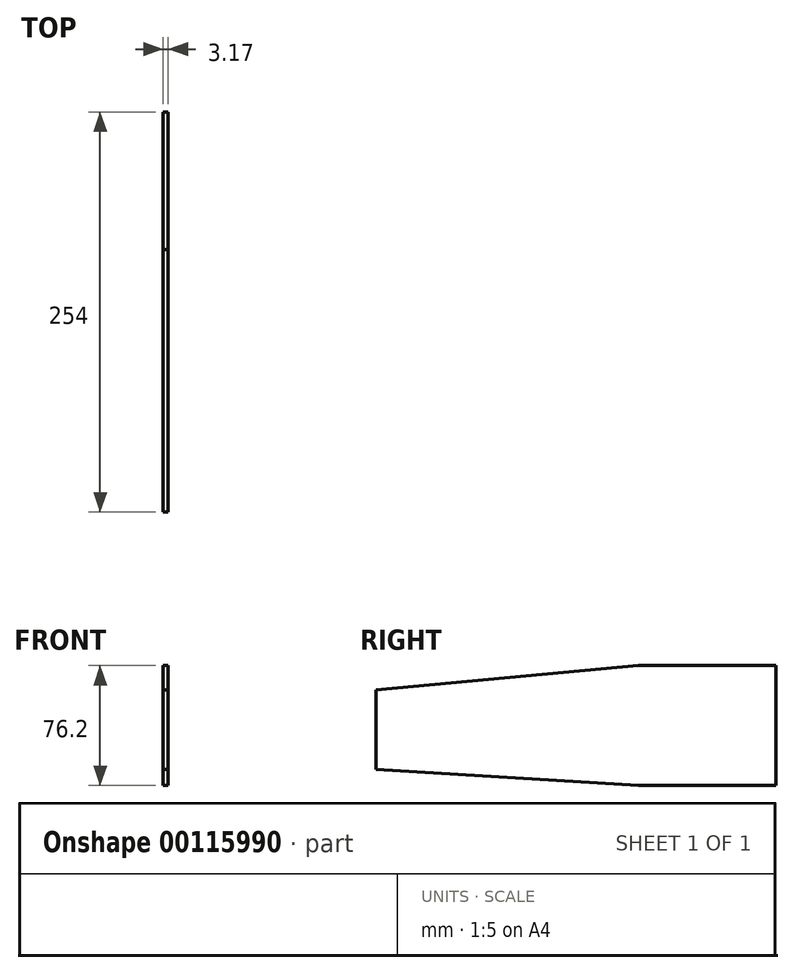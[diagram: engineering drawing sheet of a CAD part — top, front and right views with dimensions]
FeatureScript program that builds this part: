
annotation { "Feature Type Name" : "Feature", "Feature Type Description" : "" }
export const myFeature = defineFeature(function(context is Context, id is Id, definition is map)
    precondition{}
    {
        {
            var Q0;
            Q0=qCreatedBy(makeId("Right.planeOp"),FACE);
            var sketch = newSketch(context, id + "F0", { "sketchPlane" : qUnion([Q0])});
            skLineSegment(sketch, "E0", {"start": v(-5.73, 56) * mm, "end": v(-172.52, 40.6) * mm});
            skLineSegment(sketch, "E1.MirrorCS", {"start": v(-5.73, -20.2) * mm, "end": v(-172.52, -10) * mm});
            skLineSegment(sketch, "E2.bottom", {"start": v(-5.73, 56) * mm, "end": v(81.48, 56) * mm});
            skLineSegment(sketch, "E2.top", {"start": v(-5.73, -20.2) * mm, "end": v(81.48, -20.2) * mm});
            skLineSegment(sketch, "E2.right", {"start": v(81.48, 56) * mm, "end": v(81.48, -20.2) * mm});
            skLineSegment(sketch, "E3", {"start": v(-172.52, 40.6) * mm, "end": v(-172.52, -10) * mm});
            skSolve(sketch);
        }
        {
            var Q0;
            Q0=makeQuery(id+"F0.imprint","IMPRINT",FACE,{"disambiguationData":[TD([[makeQuery(id+"F0.imprint","IMPRINT",EDGE,{"derivedFrom":sQuery(id+"F0.wireOp",EDGE,"E0")}),1.0]])]});
            extrude(context, id + "F1", {"entities" : qUnion([Q0]), "depth" : 3.17 * mm});
        }
    });
